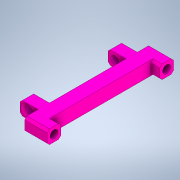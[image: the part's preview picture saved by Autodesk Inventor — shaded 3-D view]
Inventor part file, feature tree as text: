
AUTODESK INVENTOR PART (.ipt)
format: ipt  version: 2020 (Build 240168000, 168)  size: 190,464 bytes
history: native  units: mm
features: extrude x3, chamfer x3, sketch x2
ambient origin geometry x8: Origin, YZ Plane, XZ Plane, XY Plane, X Axis, Y Axis, Z Axis, Center Point
bodies: Solid1 (feature_tree)
feature tree (8):
  extrude  "Extrusion1"  Depth=6.0mm
  extrude  "Extrusion4"  Depth=6.0mm TaperAngle=0.0deg
  chamfer  "Chamfer2"  Distance=6.0mm
  sketch  "Sketch5"  dims[d4=4.0mm d6=6.0mm d7=0.0mm d19=6.0mm d22=8.0mm d24=3.5mm d25=0.0mm d26=0.0mm d27=1.0mm d28=2.0mm d29=45.0deg d33=3.5mm d34=1.0mm d35=2.0mm d36=45.0deg d37=0.0mm d38=0.0mm d39=1.0mm d40=2.0mm d41=45.0deg d42=6.0mm d43=6.0mm d45=5.0mm d46=34.0mm]
  chamfer  "Chamfer4"  Distance=8.0mm
  extrude  "Extrusion5"  Depth=34.0mm
  chamfer  "Chamfer5"  [1 undecoded]
  sketch  "Sketch4"  dims[d2=50.0mm d3=6.0mm]
note: 1 required parameter value undecoded (feature->parameter linkage not recoverable at this tier; creation-order binding heuristic only, values carry confidence <= 0.55)
